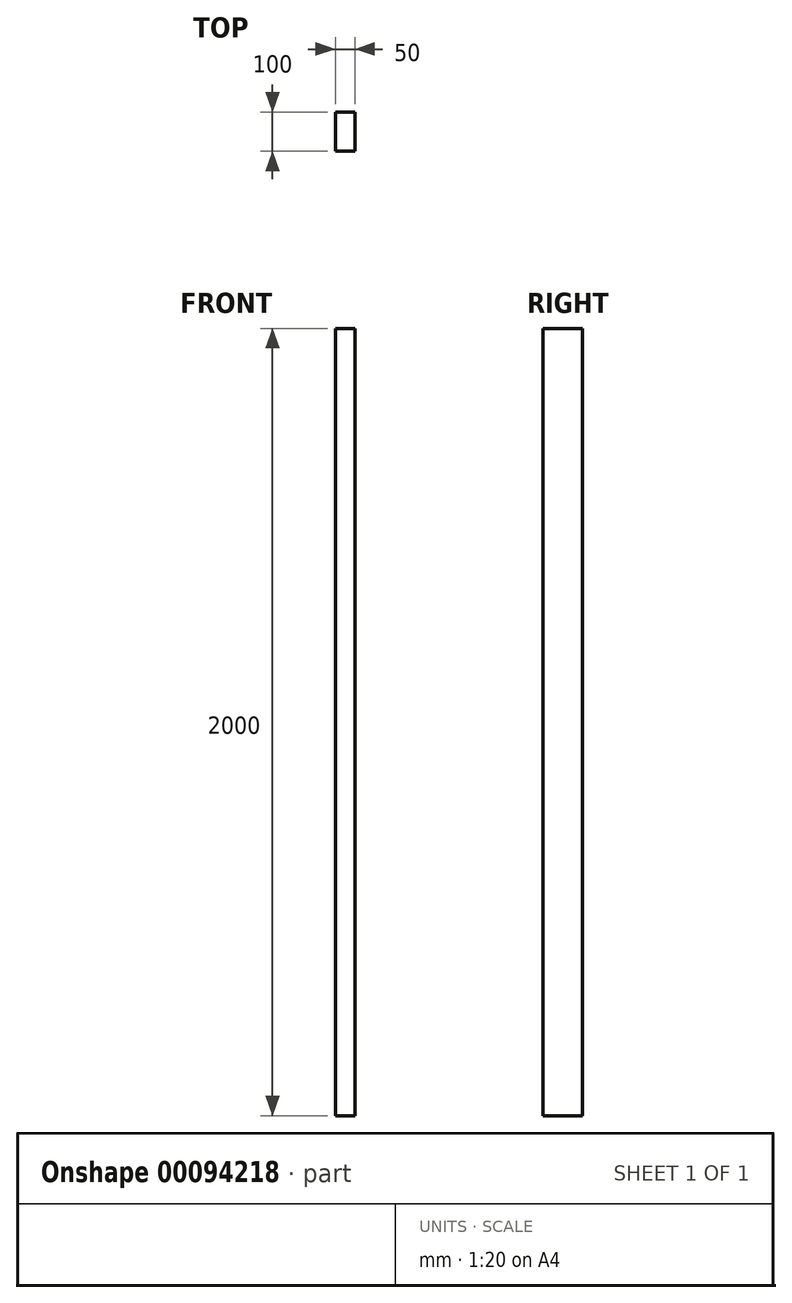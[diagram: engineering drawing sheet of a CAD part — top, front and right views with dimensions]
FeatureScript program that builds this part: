
annotation { "Feature Type Name" : "Feature", "Feature Type Description" : "" }
export const myFeature = defineFeature(function(context is Context, id is Id, definition is map)
    precondition{}
    {
        {
            var Q0;
            Q0=qCreatedBy(makeId("Front.planeOp"),FACE);
            var sketch = newSketch(context, id + "F0", { "sketchPlane" : qUnion([Q0])});
            skLineSegment(sketch, "E0.bottom", {"start": v(25, -1000) * mm, "end": v(-25, -1000) * mm});
            skLineSegment(sketch, "E0.top", {"start": v(25, 1000) * mm, "end": v(-25, 1000) * mm});
            skLineSegment(sketch, "E0.left", {"start": v(25, -1000) * mm, "end": v(25, 1000) * mm});
            skLineSegment(sketch, "E0.right", {"start": v(-25, -1000) * mm, "end": v(-25, 1000) * mm});
            skPoint(sketch, "E0.middle", {"position": v(0, 0) * mm});
            skSolve(sketch);
        }
        {
            var Q0;
            Q0=makeQuery(id+"F0.imprint","IMPRINT",FACE,{"disambiguationData":[TD([[makeQuery(id+"F0.imprint","IMPRINT",EDGE,{"derivedFrom":sQuery(id+"F0.wireOp",EDGE,"E0.bottom")}),-1.0]])]});
            extrude(context, id + "F1", {"entities" : qUnion([Q0]), "endBound" : BoundingType.SYMMETRIC, "depth" : 100 * mm});
        }
    });
